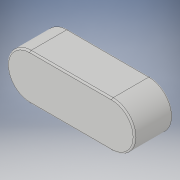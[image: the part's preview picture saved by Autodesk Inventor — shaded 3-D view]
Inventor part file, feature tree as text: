
AUTODESK INVENTOR PART (.ipt)
format: ipt  version: 2019.4 (Build 234330000, 330)  size: 116,224 bytes
history: native  units: mm
features: other x1, extrude x1, fillet x1, sketch x1
ambient origin geometry x8: Origin, YZ Plane, XZ Plane, XY Plane, X Axis, Y Axis, Z Axis, Center Point
bodies: Body1 (feature_tree)
feature tree (4):
  other  "實體1"
  extrude  "擠出1"  Depth=9.0mm
  fillet  "圓角1"  Radius=5.0mm
  sketch  "草圖1"
